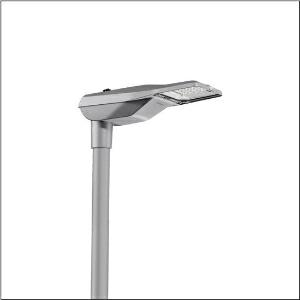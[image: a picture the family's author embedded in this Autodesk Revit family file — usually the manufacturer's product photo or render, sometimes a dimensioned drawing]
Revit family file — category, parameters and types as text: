
# Revit family: streetlight_sl_21_micro___st1_0ab_5xe1m33s08db_765d
name_source: partatom
category: Lighting Fixtures
units: mm (PartAtom-declared; Revit-internal decimal feet)

## family parameters
Cut with Voids When Loaded = No
Host = Face
Light Source = No
Part Type = Normal
Room Calculation Point = No
Round Connector Dimension = Use Diameter
Shared = No

## types (1)
- --- (1 x LED, 4500 lm, 39.1 W, 3000K)
    Apparent Load = 39 VA
    CIE Flux Codes = 38 73 97 100 100
    Color Rendering = 70
    Color Temperature = 3000K
    Default Elevation = 1800 mm
    Description = Streetlight SL 21 micro, mast luminaire, primary light control with lens, of PMMA, primary optical cover: cover, of toughened safety glass, transparent, light distribution: ST1.0aB, light emission: direct distribution, primary light characteristic: asymmetric, installation type: side-entry, post-top, LED, High Power LED, rated luminous flux: 4.500lm, luminous efficacy: 115lm/W, light colour: 730, colour temperature: 3000K, control: flexible luminous flux parameterisation, time-dependent luminous flux control, constant luminous flux control, overheat protection, pre-setting: logarithmic dimming characteristic, mains connection: 220..240V, AC, 50/60Hz, start of lifetime: 39W, end of service life: 41W, reduction: 18W, luminaire housing, of diecast aluminium, powder-coated, Siteco® metallic grey (DB 702S), corrosivity category C5 mid according to DIN EN ISO 12944, please order mast flange separately, inclination adjustable: 0°, 5°, 10°, 15°, sealing non-destructively replaceable, multi-level sealing system, length: 528mm, width: 235mm, height: 110mm, mast flange for spigot size: 42mm (side-entry): 5XC10008XM4, 60/48mm (side-entry/post-top): 5XC10108XM2, 76/60mm (side-entry/post-top): 5XC10108XM1, Smart Interface above, protection rating (complete): IP66, insulation class (complete): insulation class II (safety insulation), certification: CE, ENEC, ENEC+, VDE, impact resistance: IK09, permissible operating ambient temperature for outdoor applications: -40..+50°C, standard-compliant lighting for roads and squares, packaging unit: 1 piece

Light Distribution: ST1.0aB
    Height = 110 mm
    Lamp = 1 x LED
    Lamp Light Flux = 4500 lm
    Lamp Power = 39.1 W
    Lamp count = 1
    Length = 528 mm
    Luminous efficacy = 115 lm/W
    Manufacturer = Siteco
    ModVariant = No
    Model = 5XE1M33S08DB
    Number of Poles = 1
    OnlyDefault = Yes
    Power Factor = 1
    Product Name = Streetlight SL 21 micro | ST1.0aB
    Product group = mast luminaire | pylon top
    ProductGroupID = 6100
    Protection Class = Protection class II
    Protection Degree = IP 66
    RLX_Detail_Level = 1
    RLX_Emergency_Light_Flux = 0 lm
    RLX_Emergency_Type = 0
    RLX_Emergency_Type_DB = No
    RlxData = <blob elided: 98573 chars, md5=2c845711>
    Socket = socket
    Standby Power = 0 W
    System Light Flux = 4500 lm
    System Power = 39 W
    Type Comments = factory setting: luminous flux: 100 % | dim-lin: 254 | 765 mA
    Type Image = l_1277292.jpg
    URL = http://relux.com
    VarID = @adj_124349
    Voltage = 0 V
    Weight = 0.00 kg
    Width = 235 mm

## geometry (parser evidence)
native form markers: Blend x4, Sweep x10
no freeform markers — native parametric forms only
